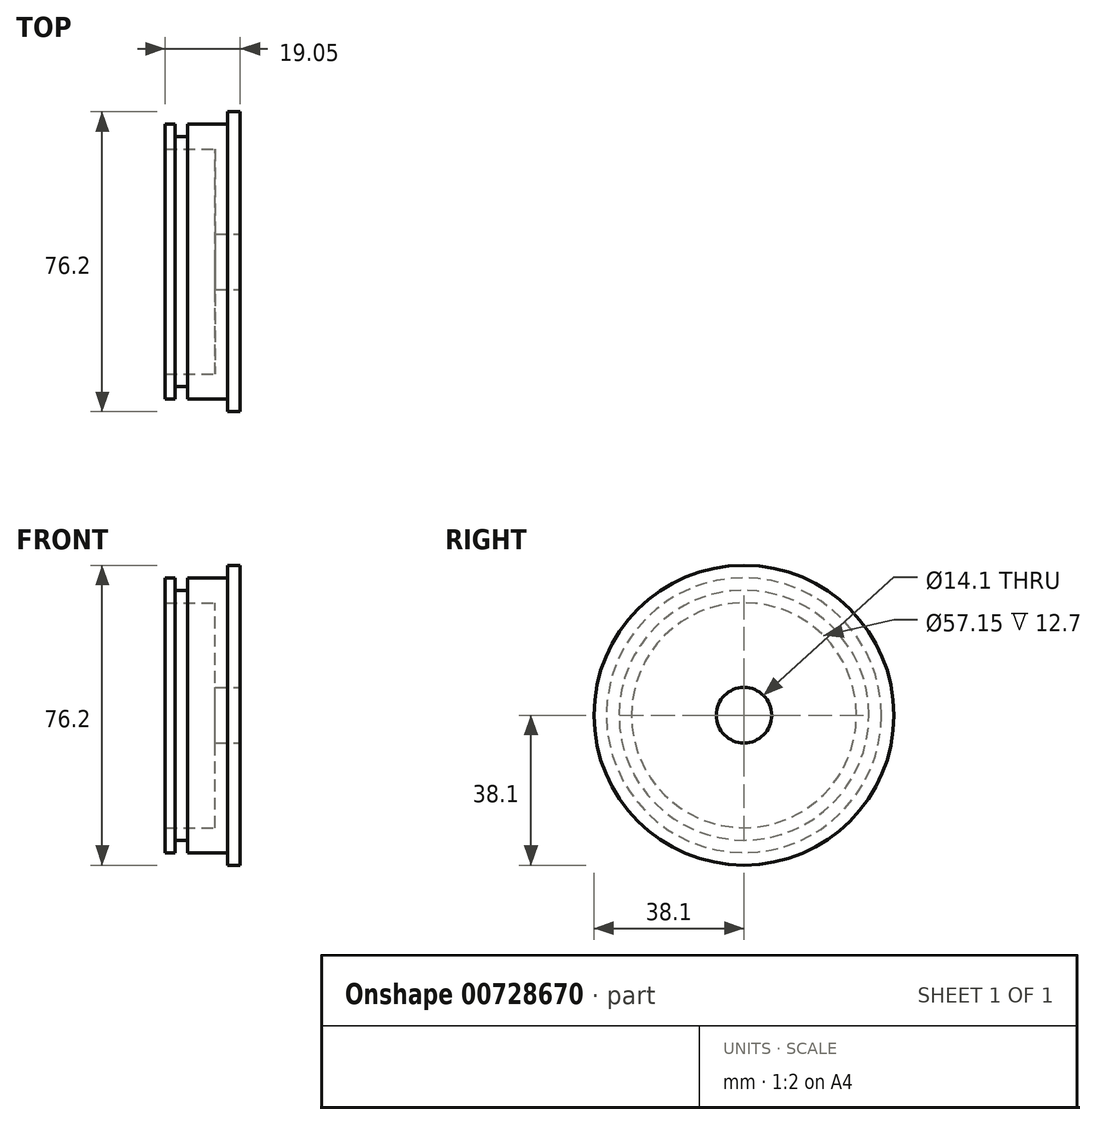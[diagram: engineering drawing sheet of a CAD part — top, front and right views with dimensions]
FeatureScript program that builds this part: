
annotation { "Feature Type Name" : "Feature", "Feature Type Description" : "" }
export const myFeature = defineFeature(function(context is Context, id is Id, definition is map)
    precondition{}
    {
        {
            var Q0;
            Q0=qCreatedBy(makeId("Front.planeOp"),FACE);
            var sketch = newSketch(context, id + "F0", { "sketchPlane" : qUnion([Q0])});
            skLineSegment(sketch, "E0", {"start": v(-6.59, 7.05) * mm, "end": v(-6.59, 28.58) * mm});
            skLineSegment(sketch, "E1", {"start": v(-6.59, 28.58) * mm, "end": v(-19.29, 28.58) * mm});
            skLineSegment(sketch, "E2", {"start": v(-19.29, 28.58) * mm, "end": v(-19.29, 34.92) * mm});
            skLineSegment(sketch, "E3", {"start": v(-19.29, 34.92) * mm, "end": v(-16.75, 34.92) * mm});
            skLineSegment(sketch, "E4", {"start": v(-16.75, 34.93) * mm, "end": v(-16.75, 31.75) * mm});
            skLineSegment(sketch, "E5", {"start": v(-16.75, 31.75) * mm, "end": v(-13.57, 31.75) * mm});
            skLineSegment(sketch, "E6", {"start": v(-13.57, 31.75) * mm, "end": v(-13.57, 34.93) * mm});
            skLineSegment(sketch, "E7", {"start": v(-13.57, 34.92) * mm, "end": v(-3.41, 34.92) * mm});
            skLineSegment(sketch, "E8", {"start": v(-3.41, 34.93) * mm, "end": v(-3.41, 38.1) * mm});
            skLineSegment(sketch, "E9", {"start": v(-3.41, 38.1) * mm, "end": v(-0.24, 38.1) * mm});
            skLineSegment(sketch, "E10", {"start": v(-0.24, 38.1) * mm, "end": v(-0.24, 7.05) * mm});
            skLineSegment(sketch, "E11", {"start": v(-6.59, 7.05) * mm, "end": v(-0.24, 7.05) * mm});
            skPoint(sketch, "E12.orphan", {"position": v(-6.59, 0) * mm});
            skPoint(sketch, "E13.orphan", {"position": v(-0.24, 0) * mm});
            skLineSegment(sketch, "E14", {"start": v(-0.24, 0) * mm, "end": v(-6.59, 0) * mm, "construction": true});
            skSolve(sketch);
        }
        {
            var Q0;
            Q0 = qSketchRegion(id + "F0", true);
            var Q1;
            Q1=sQuery(id+"F0.wireOp",EDGE,"E14");
            revolve(context, id + "F1", {"surfaceOperationType" : NewSurfaceOperationType.NEW, "entities" : qUnion([Q0]), "axis" : qUnion([Q1]), "revolveType" : RevolveType.FULL});
        }
    });
